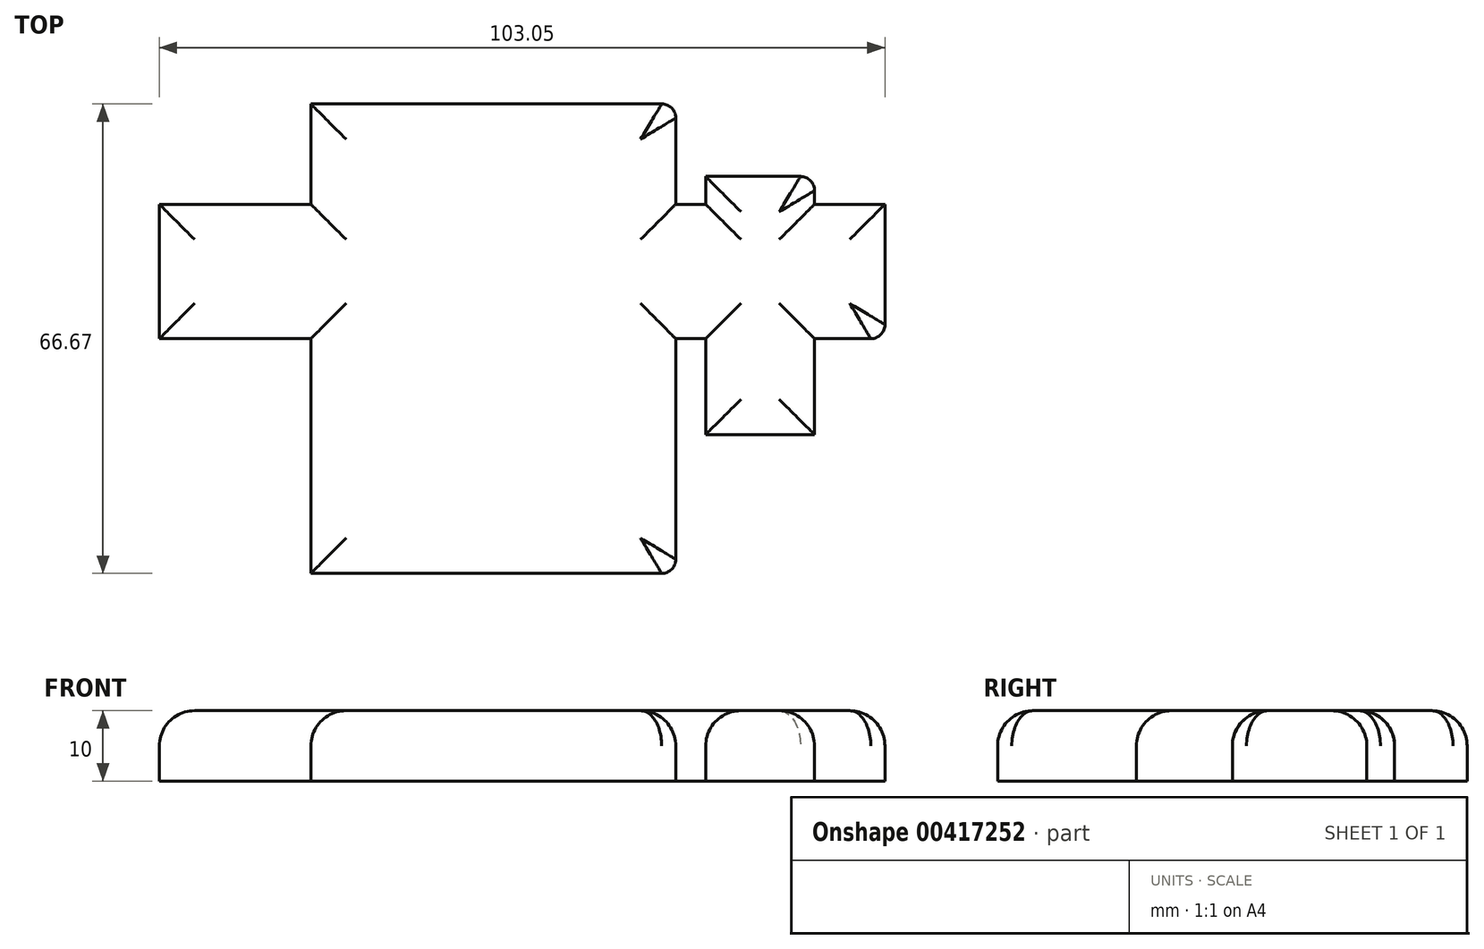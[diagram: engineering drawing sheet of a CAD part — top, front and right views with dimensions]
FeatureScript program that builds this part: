
annotation { "Feature Type Name" : "Feature", "Feature Type Description" : "" }
export const myFeature = defineFeature(function(context is Context, id is Id, definition is map)
    precondition{}
    {
        {
            var Q0;
            Q0=qCreatedBy(makeId("Top.planeOp"),FACE);
            var sketch = newSketch(context, id + "F0", { "sketchPlane" : qUnion([Q0])});
            skLineSegment(sketch, "E0.bottom", {"start": v(-56.07, 18.18) * mm, "end": v(-4.24, 18.18) * mm});
            skLineSegment(sketch, "E0.top", {"start": v(-56.07, -48.5) * mm, "end": v(-4.24, -48.5) * mm});
            skLineSegment(sketch, "E0.left", {"start": v(-56.07, 18.18) * mm, "end": v(-56.07, -48.5) * mm});
            skLineSegment(sketch, "E0.right", {"start": v(-4.24, 18.18) * mm, "end": v(-4.24, -48.5) * mm});
            skLineSegment(sketch, "E1.bottom", {"start": v(15.46, 7.88) * mm, "end": v(0, 7.88) * mm});
            skLineSegment(sketch, "E1.top", {"start": v(15.46, -28.8) * mm, "end": v(0, -28.8) * mm});
            skLineSegment(sketch, "E1.left", {"start": v(15.46, 7.88) * mm, "end": v(15.46, -28.8) * mm});
            skLineSegment(sketch, "E1.right", {"start": v(0, 7.88) * mm, "end": v(0, -28.8) * mm});
            skLineSegment(sketch, "E2.bottom", {"start": v(-77.59, 3.94) * mm, "end": v(25.46, 3.94) * mm});
            skLineSegment(sketch, "E2.top", {"start": v(-77.59, -15.15) * mm, "end": v(25.46, -15.15) * mm});
            skLineSegment(sketch, "E2.left", {"start": v(-77.59, 3.94) * mm, "end": v(-77.59, -15.15) * mm});
            skLineSegment(sketch, "E2.right", {"start": v(25.46, 3.94) * mm, "end": v(25.46, -15.15) * mm});
            skSolve(sketch);
        }
        {
            var Q0;
            Q0 = qSketchRegion(id + "F0", true);
            extrude(context, id + "F1", {"entities" : qUnion([Q0]), "depth" : 10 * mm});
        }
        {
            var Q0;
            Q0=makeQuery(id+"F1.opExtrude","SWEPT_EDGE",EDGE,{"disambiguationData":[OSD([sQuery(id+"F0.wireOp",EDGE,"E0.top"),sQuery(id+"F0.wireOp",EDGE,"E0.right")])]});
            var Q1;
            Q1=makeQuery(id+"F1.opExtrude","SWEPT_EDGE",EDGE,{"disambiguationData":[OSD([sQuery(id+"F0.wireOp",EDGE,"E2.top"),sQuery(id+"F0.wireOp",EDGE,"E2.right")])]});
            var Q2;
            Q2=makeQuery(id+"F1.opExtrude","SWEPT_EDGE",EDGE,{"disambiguationData":[OSD([sQuery(id+"F0.wireOp",EDGE,"E1.bottom"),sQuery(id+"F0.wireOp",EDGE,"E1.left")])]});
            var Q3;
            Q3=makeQuery(id+"F1.opExtrude","SWEPT_EDGE",EDGE,{"disambiguationData":[OSD([sQuery(id+"F0.wireOp",EDGE,"E0.bottom"),sQuery(id+"F0.wireOp",EDGE,"E0.right")])]});
            fillet(context, id + "F2", {"entities" : qUnion([Q0, Q1, Q2, Q3]), "radius" : 2 * mm, "tangentPropagation" : true, "allowEdgeOverflow" : false});
        }
        {
            var Q0;
            Q0=makeQuery(id+"F1.opExtrude","CAP_FACE",FACE,{"disambiguationData":[OSD([sQuery(id+"F0.wireOp",EDGE,"E0.bottom"),sQuery(id+"F0.wireOp",EDGE,"E0.top"),sQuery(id+"F0.wireOp",EDGE,"E0.left"),sQuery(id+"F0.wireOp",EDGE,"E0.right"),sQuery(id+"F0.wireOp",EDGE,"E1.bottom"),sQuery(id+"F0.wireOp",EDGE,"E1.top"),sQuery(id+"F0.wireOp",EDGE,"E1.left"),sQuery(id+"F0.wireOp",EDGE,"E1.right"),sQuery(id+"F0.wireOp",EDGE,"E2.bottom"),sQuery(id+"F0.wireOp",EDGE,"E2.top"),sQuery(id+"F0.wireOp",EDGE,"E2.left"),sQuery(id+"F0.wireOp",EDGE,"E2.right")])],"isStart":false});
            fillet(context, id + "F3", {"entities" : qUnion([Q0]), "radius" : 5 * mm, "tangentPropagation" : true, "allowEdgeOverflow" : false});
        }
    });
